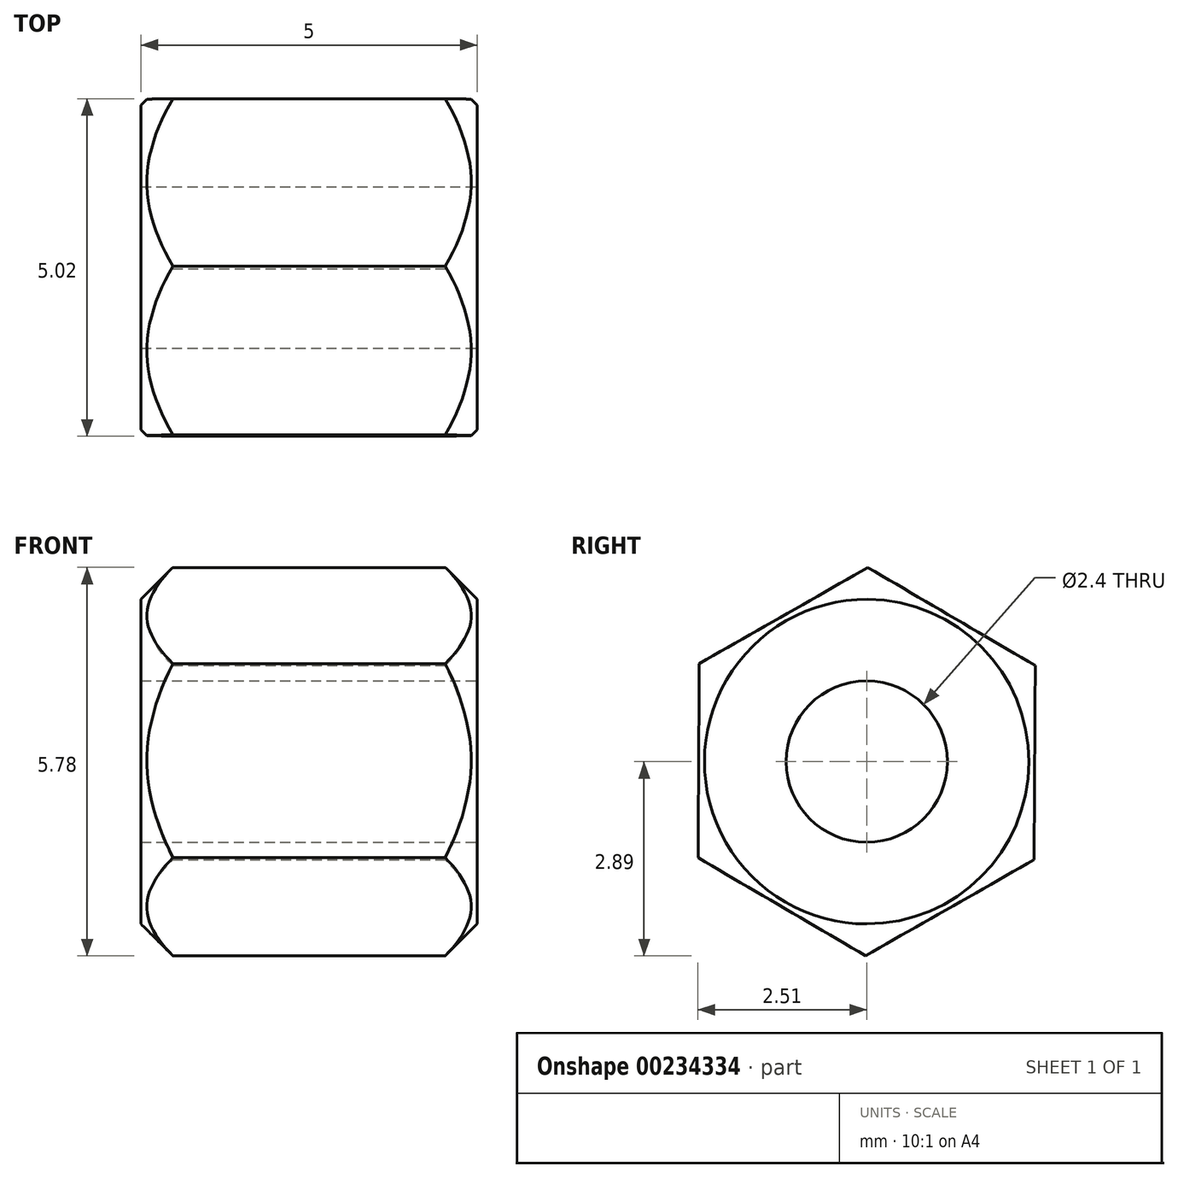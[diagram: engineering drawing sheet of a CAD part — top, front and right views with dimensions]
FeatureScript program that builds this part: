
annotation { "Feature Type Name" : "Feature", "Feature Type Description" : "" }
export const myFeature = defineFeature(function(context is Context, id is Id, definition is map)
    precondition{}
    {
        {
            var Q0;
            Q0=qCreatedBy(makeId("Right.planeOp"),FACE);
            var sketch = newSketch(context, id + "F0", { "sketchPlane" : qUnion([Q0])});
            skCircle(sketch, "E0.cCircle", {"center": v(0, 0) * mm, "radius": 2.5 * mm, "construction": true});
            skLineSegment(sketch, "E0.0", {"start": v(2.5, -1.46) * mm, "end": v(-0.02, -2.89) * mm});
            skLineSegment(sketch, "E0.1", {"start": v(-0.02, -2.89) * mm, "end": v(-2.5, -1.43) * mm});
            skLineSegment(sketch, "E0.2", {"start": v(-2.5, -1.43) * mm, "end": v(-2.5, 1.46) * mm});
            skLineSegment(sketch, "E0.3", {"start": v(-2.5, 1.46) * mm, "end": v(0.02, 2.89) * mm});
            skLineSegment(sketch, "E0.4", {"start": v(0.02, 2.89) * mm, "end": v(2.5, 1.43) * mm});
            skLineSegment(sketch, "E0.5", {"start": v(2.5, 1.43) * mm, "end": v(2.5, -1.46) * mm});
            skPoint(sketch, "E0.0.midPoint", {"position": v(1.24, -2.17) * mm});
            skCircle(sketch, "E1", {"center": v(0, 0) * mm, "radius": 1.2 * mm});
            skSolve(sketch);
        }
        {
            var Q0;
            Q0=makeQuery(id+"F0.imprint","IMPRINT",FACE,{"disambiguationData":[TD([[makeQuery(id+"F0.imprint","IMPRINT",EDGE,{"derivedFrom":sQuery(id+"F0.wireOp",EDGE,"E0.0")}),-1.0]])]});
            extrude(context, id + "F1", {"entities" : qUnion([Q0]), "oppositeDirection" : true, "depth" : 5 * mm, "offsetDistance" : 25 * mm, "symmetric" : true});
        }
        {
            var Q0;
            Q0=qCreatedBy(makeId("Front.planeOp"),FACE);
            var sketch = newSketch(context, id + "F2", { "sketchPlane" : qUnion([Q0])});
            skLineSegment(sketch, "E2", {"start": v(3.24, -1.68) * mm, "end": v(3.24, -3.68) * mm});
            skLineSegment(sketch, "E3", {"start": v(3.24, -3.68) * mm, "end": v(1.24, -3.68) * mm});
            skLineSegment(sketch, "E4", {"start": v(1.24, -3.68) * mm, "end": v(3.24, -1.68) * mm});
            skLineSegment(sketch, "E5", {"start": v(9.88, 0) * mm, "end": v(-9.88, 0) * mm});
            skLineSegment(sketch, "E6", {"start": v(0, 0) * mm, "end": v(0, -4.96) * mm, "construction": true});
            skPoint(sketch, "E6.endSnap0", {"position": v(0, 0) * mm});
            skLineSegment(sketch, "E7.MirrorCS", {"start": v(-3.24, -3.68) * mm, "end": v(-1.24, -3.68) * mm});
            skLineSegment(sketch, "E8.MirrorCS", {"start": v(-3.24, -1.68) * mm, "end": v(-3.24, -3.68) * mm});
            skLineSegment(sketch, "E9.MirrorCS", {"start": v(-1.24, -3.68) * mm, "end": v(-3.24, -1.68) * mm});
            skSolve(sketch);
        }
        {
            var Q0;
            Q0=makeQuery(id+"F2.imprint","IMPRINT",FACE,{"disambiguationData":[TD([[makeQuery(id+"F2.imprint","IMPRINT",EDGE,{"derivedFrom":sQuery(id+"F2.wireOp",EDGE,"E2")}),-1.0]])]});
            var Q1;
            Q1=makeQuery(id+"F2.imprint","IMPRINT",FACE,{"disambiguationData":[TD([[makeQuery(id+"F2.imprint","IMPRINT",EDGE,{"derivedFrom":sQuery(id+"F2.wireOp",EDGE,"E7.MirrorCS")}),1.0]])]});
            var Q2;
            Q2=sQuery(id+"F2.wireOp",EDGE,"E4");
            var Q3;
            Q3=sQuery(id+"F2.wireOp",EDGE,"E5");
            revolve(context, id + "F3", {"operationType" : NewBodyOperationType.REMOVE, "entities" : qUnion([Q0, Q1]), "surfaceEntities" : qUnion([Q2]), "axis" : qUnion([Q3]), "revolveType" : RevolveType.FULL, "oppositeDirection" : true});
        }
    });
